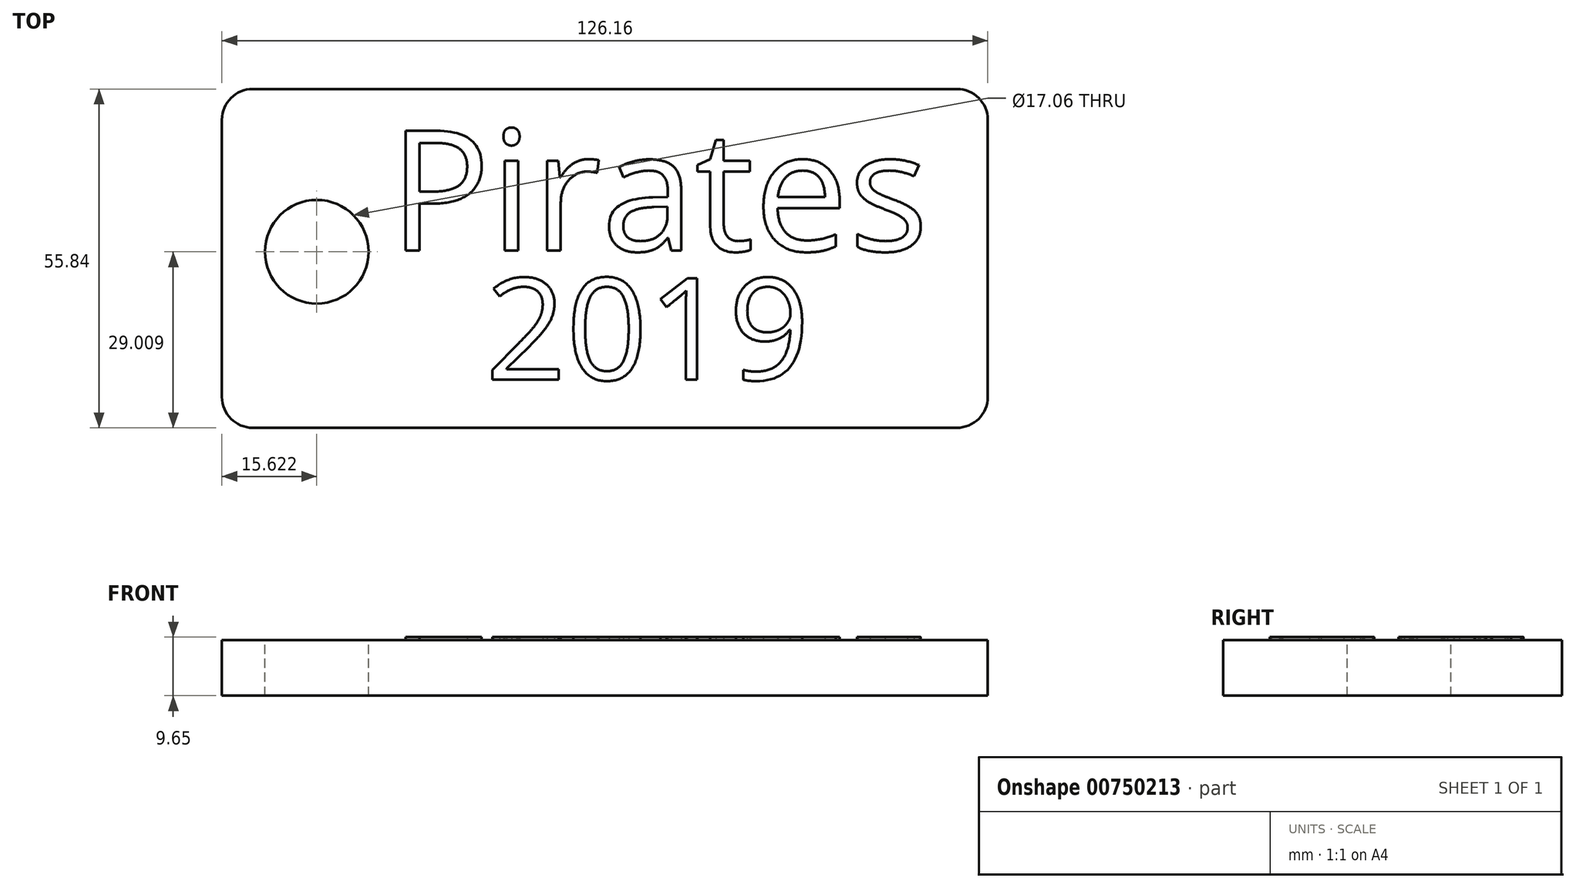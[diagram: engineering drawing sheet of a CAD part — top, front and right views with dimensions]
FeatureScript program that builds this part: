
annotation { "Feature Type Name" : "Feature", "Feature Type Description" : "" }
export const myFeature = defineFeature(function(context is Context, id is Id, definition is map)
    precondition{}
    {
        {
            var Q0;
            Q0=qCreatedBy(makeId("Top.planeOp"),FACE);
            var sketch = newSketch(context, id + "F0", { "sketchPlane" : qUnion([Q0])});
            skLineSegment(sketch, "E0.bottom", {"start": v(-61.1, 33.96) * mm, "end": v(65.06, 33.96) * mm});
            skLineSegment(sketch, "E0.top", {"start": v(-61.1, -21.88) * mm, "end": v(65.06, -21.88) * mm});
            skLineSegment(sketch, "E0.left", {"start": v(-61.1, 33.96) * mm, "end": v(-61.1, -21.88) * mm});
            skLineSegment(sketch, "E0.right", {"start": v(65.06, 33.96) * mm, "end": v(65.06, -21.88) * mm});
            skSolve(sketch);
        }
        {
            var Q0;
            Q0=makeQuery(id+"F0.imprint","IMPRINT",FACE,{"disambiguationData":[TD([[makeQuery(id+"F0.imprint","IMPRINT",EDGE,{"derivedFrom":sQuery(id+"F0.wireOp",EDGE,"E0.bottom")}),-1.0]])]});
            extrude(context, id + "F1", {"entities" : qUnion([Q0]), "depth" : 9.14 * mm, "offsetDistance" : 25.4 * mm});
        }
        {
            var Q0;
            Q0=makeQuery(id+"F1.opExtrude","CAP_FACE",FACE,{"disambiguationData":[OSD([sQuery(id+"F0.wireOp",EDGE,"E0.bottom"),sQuery(id+"F0.wireOp",EDGE,"E0.top"),sQuery(id+"F0.wireOp",EDGE,"E0.left"),sQuery(id+"F0.wireOp",EDGE,"E0.right")])],"isStart":false});
            var sketch = newSketch(context, id + "F2", { "sketchPlane" : qUnion([Q0])});
            skCircle(sketch, "E1", {"center": v(-45.48, 7.13) * mm, "radius": 8.53 * mm});
            skSolve(sketch);
        }
        {
            var Q0;
            Q0=makeQuery(id+"F2.imprint","IMPRINT",FACE,{"disambiguationData":[TD([[makeQuery(id+"F2.imprint","IMPRINT",EDGE,{"derivedFrom":sQuery(id+"F2.wireOp",EDGE,"E1")}),1.0]])]});
            extrude(context, id + "F3", {"entities" : qUnion([Q0]), "operationType" : NewBodyOperationType.REMOVE, "oppositeDirection" : true, "depth" : 25.4 * mm, "offsetDistance" : 25.4 * mm});
        }
        {
            var Q0;
            Q0=makeQuery(id+"F1.opExtrude","SWEPT_EDGE",EDGE,{"disambiguationData":[OSD([sQuery(id+"F0.wireOp",EDGE,"E0.top"),sQuery(id+"F0.wireOp",EDGE,"E0.right")])]});
            fillet(context, id + "F4", {"entities" : qUnion([Q0]), "radius" : 5.08 * mm, "tangentPropagation" : true, "allowEdgeOverflow" : false});
        }
        {
            var Q0;
            Q0=makeQuery(id+"F1.opExtrude","SWEPT_EDGE",EDGE,{"disambiguationData":[OSD([sQuery(id+"F0.wireOp",EDGE,"E0.bottom"),sQuery(id+"F0.wireOp",EDGE,"E0.right")])]});
            fillet(context, id + "F5", {"entities" : qUnion([Q0]), "radius" : 5.08 * mm, "tangentPropagation" : true, "allowEdgeOverflow" : false});
        }
        {
            var Q0;
            Q0=makeQuery(id+"F1.opExtrude","SWEPT_EDGE",EDGE,{"disambiguationData":[OSD([sQuery(id+"F0.wireOp",EDGE,"E0.top"),sQuery(id+"F0.wireOp",EDGE,"E0.left")])]});
            fillet(context, id + "F6", {"entities" : qUnion([Q0]), "radius" : 5.08 * mm, "tangentPropagation" : true, "allowEdgeOverflow" : false});
        }
        {
            var Q0;
            Q0=makeQuery(id+"F1.opExtrude","SWEPT_EDGE",EDGE,{"disambiguationData":[OSD([sQuery(id+"F0.wireOp",EDGE,"E0.bottom"),sQuery(id+"F0.wireOp",EDGE,"E0.left")])]});
            fillet(context, id + "F7", {"entities" : qUnion([Q0]), "radius" : 5.08 * mm, "tangentPropagation" : true, "allowEdgeOverflow" : false});
        }
        {
            var Q0;
            Q0=makeQuery(id+"F1.opExtrude","CAP_FACE",FACE,{"disambiguationData":[OSD([sQuery(id+"F0.wireOp",EDGE,"E0.bottom"),sQuery(id+"F0.wireOp",EDGE,"E0.top"),sQuery(id+"F0.wireOp",EDGE,"E0.left"),sQuery(id+"F0.wireOp",EDGE,"E0.right")])],"isStart":false});
            var sketch = newSketch(context, id + "F8", { "sketchPlane" : qUnion([Q0])});
            skText(sketch, "E2", { "text": "Pirates", "fontName": "OpenSans-Regular.ttf"});
            skText(sketch, "E3", { "text": "2019", "fontName": "OpenSans-Regular.ttf"});
            const initialGuessF8  = {"E2": [-0.03357, 0.0073, 1, 0, 0.01993], "E3": [-0.01772, -0.01396, 1, 0, 0.01683]};
            skSetInitialGuess(sketch, initialGuessF8);
            skSolve(sketch);
        }
        {
            var Q0;
            Q0 = qSketchRegion(id + "F8", true);
            extrude(context, id + "F9", {"entities" : qUnion([Q0]), "operationType" : NewBodyOperationType.ADD, "depth" : 0.5 * mm, "offsetDistance" : 25.4 * mm});
        }
    });
